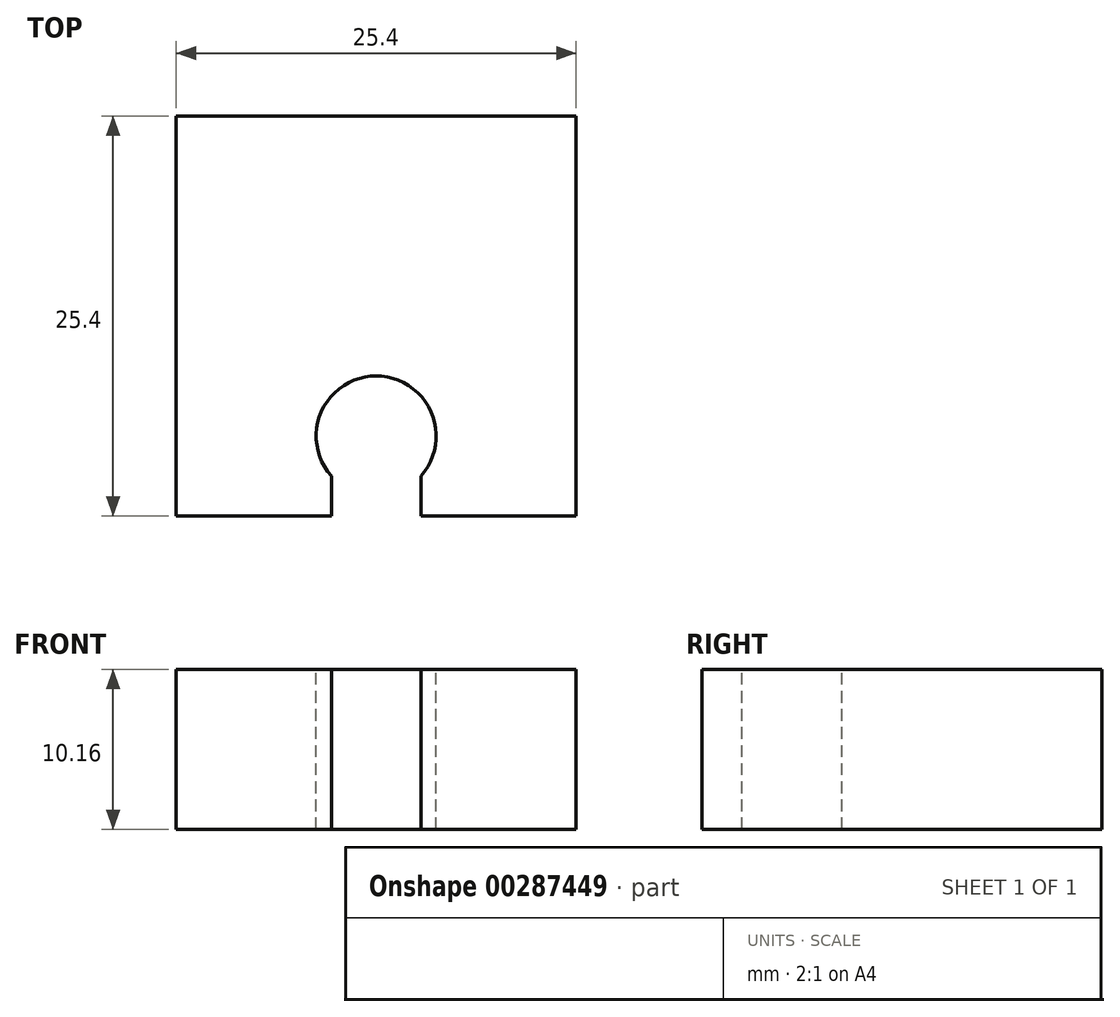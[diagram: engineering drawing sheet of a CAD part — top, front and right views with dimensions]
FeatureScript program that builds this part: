
annotation { "Feature Type Name" : "Feature", "Feature Type Description" : "" }
export const myFeature = defineFeature(function(context is Context, id is Id, definition is map)
    precondition{}
    {
        {
            var Q0;
            Q0=qCreatedBy(makeId("Top.planeOp"),FACE);
            var sketch = newSketch(context, id + "F0", { "sketchPlane" : qUnion([Q0])});
            skLineSegment(sketch, "E0.bottom", {"start": v(12.7, -12.7) * mm, "end": v(-12.7, -12.7) * mm});
            skLineSegment(sketch, "E0.top", {"start": v(12.7, 12.7) * mm, "end": v(-12.7, 12.7) * mm});
            skLineSegment(sketch, "E0.left", {"start": v(12.7, -12.7) * mm, "end": v(12.7, 12.7) * mm});
            skLineSegment(sketch, "E0.right", {"start": v(-12.7, -12.7) * mm, "end": v(-12.7, 12.7) * mm});
            skPoint(sketch, "E0.middle", {"position": v(0, 0) * mm});
            skSolve(sketch);
        }
        {
            var Q0;
            Q0 = qSketchRegion(id + "F0", true);
            extrude(context, id + "F1", {"entities" : qUnion([Q0]), "depth" : 10.16 * mm});
        }
        {
            var Q0;
            Q0=makeQuery(id+"F1.opExtrude","CAP_FACE",FACE,{"disambiguationData":[OSD([sQuery(id+"F0.wireOp",EDGE,"E0.bottom"),sQuery(id+"F0.wireOp",EDGE,"E0.top"),sQuery(id+"F0.wireOp",EDGE,"E0.left"),sQuery(id+"F0.wireOp",EDGE,"E0.right")])],"isStart":false});
            var sketch = newSketch(context, id + "F2", { "sketchPlane" : qUnion([Q0])});
            skCircle(sketch, "E1", {"center": v(0, -7.62) * mm, "radius": 3.81 * mm});
            skSolve(sketch);
        }
        {
            var Q0;
            Q0 = qSketchRegion(id + "F2", true);
            extrude(context, id + "F3", {"entities" : qUnion([Q0]), "operationType" : NewBodyOperationType.REMOVE, "oppositeDirection" : true, "depth" : 25.4 * mm});
        }
        {
            var Q0;
            Q0=makeQuery(id+"F1.opExtrude","CAP_FACE",FACE,{"disambiguationData":[OSD([sQuery(id+"F0.wireOp",EDGE,"E0.bottom"),sQuery(id+"F0.wireOp",EDGE,"E0.top"),sQuery(id+"F0.wireOp",EDGE,"E0.left"),sQuery(id+"F0.wireOp",EDGE,"E0.right")])],"isStart":false});
            var sketch = newSketch(context, id + "F4", { "sketchPlane" : qUnion([Q0])});
            skLineSegment(sketch, "E2.bottom", {"start": v(-2.84, -12.7) * mm, "end": v(2.84, -12.7) * mm});
            skLineSegment(sketch, "E2.top", {"start": v(-2.84, -10.16) * mm, "end": v(2.84, -10.16) * mm, "construction": true});
            skLineSegment(sketch, "E2.left", {"start": v(-2.84, -12.7) * mm, "end": v(-2.84, -10.16) * mm});
            skLineSegment(sketch, "E2.right", {"start": v(2.84, -12.7) * mm, "end": v(2.84, -10.16) * mm});
            skLineSegment(sketch, "E3", {"start": v(-2.84, -11.43) * mm, "end": v(0, -11.43) * mm, "construction": true});
            skLineSegment(sketch, "E4", {"start": v(0, -11.43) * mm, "end": v(0, -10.16) * mm, "construction": true});
            skArc(sketch, "E5", {"start": v(-2.84, -10.16) * mm, "mid": v(0, -11.43) * mm, "end": v(2.84, -10.16) * mm});
            skSolve(sketch);
        }
        {
            var Q0;
            Q0=makeQuery(id+"F4.imprint","IMPRINT",FACE,{"disambiguationData":[TD([[makeQuery(id+"F4.imprint","IMPRINT",EDGE,{"derivedFrom":sQuery(id+"F4.wireOp",EDGE,"E2.bottom")}),-1.0]])]});
            extrude(context, id + "F5", {"entities" : qUnion([Q0]), "operationType" : NewBodyOperationType.REMOVE, "oppositeDirection" : true, "depth" : 25.4 * mm});
        }
        {
            var Q0;
            Q0=qCreatedBy(makeId("Front.planeOp"),FACE);
            var sketch = newSketch(context, id + "F6", { "sketchPlane" : qUnion([Q0])});
            skLineSegment(sketch, "E6", {"start": v(0, 0) * mm, "end": v(0, 12.7) * mm, "construction": true});
            skSolve(sketch);
        }
    });
